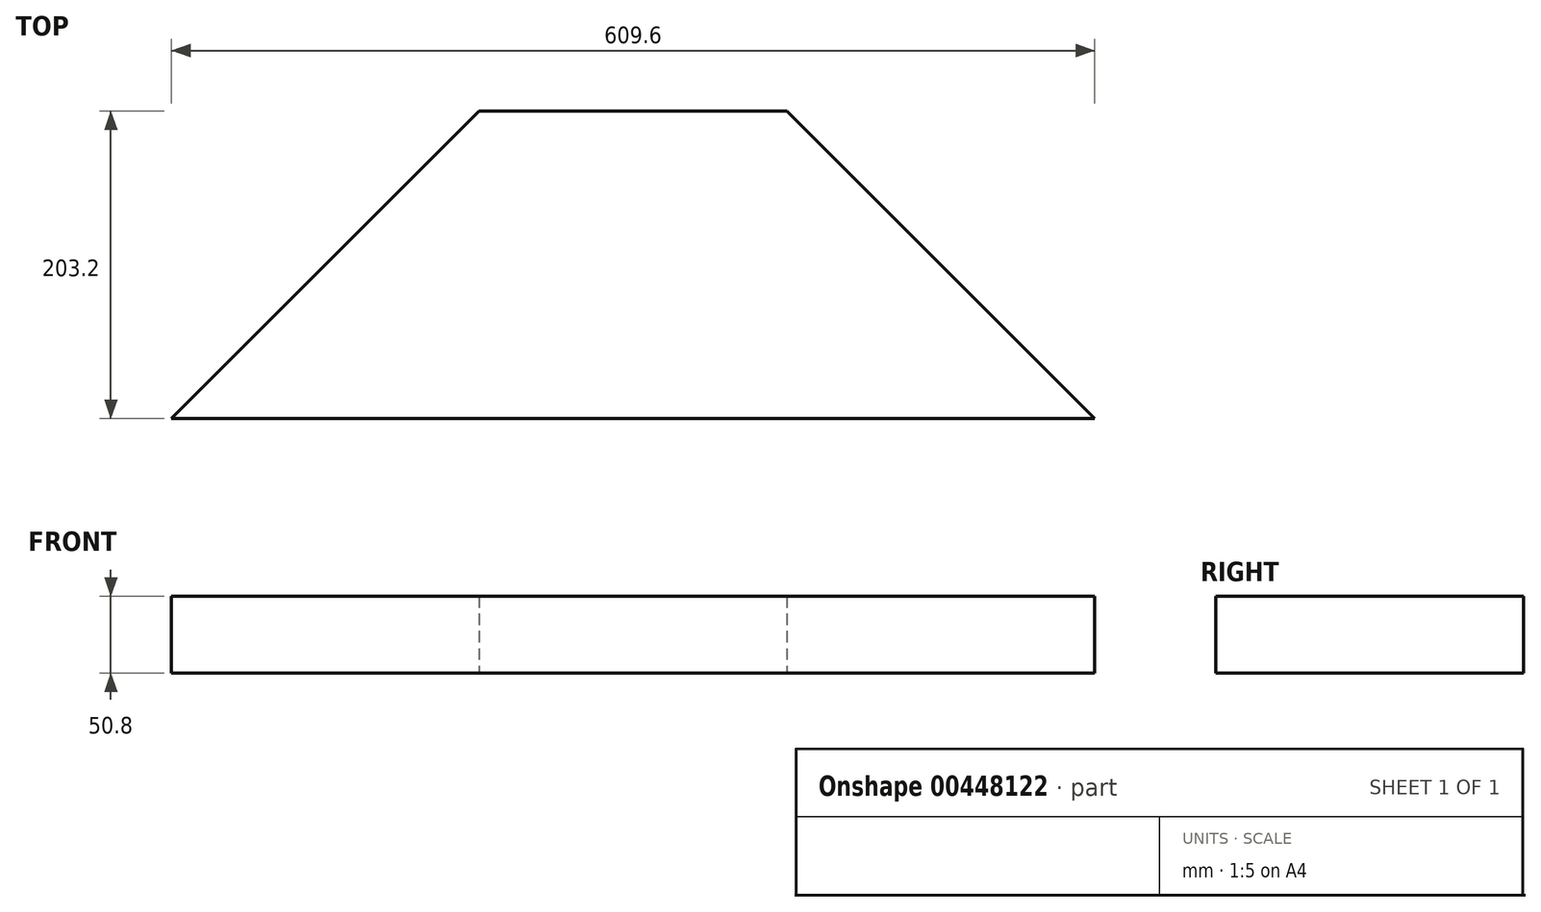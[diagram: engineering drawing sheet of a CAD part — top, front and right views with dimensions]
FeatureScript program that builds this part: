
annotation { "Feature Type Name" : "Feature", "Feature Type Description" : "" }
export const myFeature = defineFeature(function(context is Context, id is Id, definition is map)
    precondition{}
    {
        {
            var Q0;
            Q0=qCreatedBy(makeId("Top.planeOp"),FACE);
            var sketch = newSketch(context, id + "F0", { "sketchPlane" : qUnion([Q0])});
            skPoint(sketch, "E0", {"position": v(0, 203.2) * mm});
            skPoint(sketch, "E1", {"position": v(101.6, 203.2) * mm});
            skPoint(sketch, "E2", {"position": v(-101.6, 203.2) * mm});
            skPoint(sketch, "E3", {"position": v(304.8, 0) * mm});
            skPoint(sketch, "E4", {"position": v(-304.8, 0) * mm});
            skLineSegment(sketch, "E5", {"start": v(-101.6, 203.2) * mm, "end": v(101.6, 203.2) * mm});
            skLineSegment(sketch, "E6", {"start": v(304.8, 0) * mm, "end": v(-304.8, 0) * mm});
            skLineSegment(sketch, "E7", {"start": v(-304.8, 0) * mm, "end": v(-101.6, 203.2) * mm});
            skLineSegment(sketch, "E8", {"start": v(101.6, 203.2) * mm, "end": v(304.8, 0) * mm});
            skPoint(sketch, "E9", {"position": v(-203.2, 101.6) * mm});
            skPoint(sketch, "E10", {"position": v(203.2, 101.6) * mm});
            skSolve(sketch);
        }
        {
            var Q0;
            Q0=qCreatedBy(makeId("Right.planeOp"),FACE);
            var sketch = newSketch(context, id + "F1", { "sketchPlane" : qUnion([Q0])});
            skLineSegment(sketch, "E11", {"start": v(0, 0) * mm, "end": v(305.13, 152.96) * mm});
            skLineSegment(sketch, "E12", {"start": v(305.13, 152.96) * mm, "end": v(0, 152.96) * mm});
            skLineSegment(sketch, "E13", {"start": v(0, 152.96) * mm, "end": v(0, 0) * mm});
            skSolve(sketch);
        }
        {
            var Q0;
            {var subQ0=sQuery(id+"F1.wireOp",EDGE,"E11");Q0=makeQuery(id+"FYI99B2akjMyhfM_1.boolean.opBoolean","MERGE",FACE,{"derivedFrom":[makeQuery(id+"Fa1wFBmMVlfcbIP_1.boolean.opBoolean","COPY",FACE,{"derivedFrom":makeQuery(id+"Fa1wFBmMVlfcbIP_1.opExtrude","SWEPT_FACE",FACE,{"disambiguationData":[OSD([subQ0])]})}),makeQuery(id+"FYI99B2akjMyhfM_1.opExtrude","SWEPT_FACE",FACE,{"disambiguationData":[OSD([subQ0]),TDD([makeQuery(id+"F1.imprint","IMPRINT",EDGE,{"derivedFrom":subQ0})])]}),makeQuery(id+"FYI99B2akjMyhfM_1.opExtrude","SWEPT_FACE",FACE,{"disambiguationData":[OSD([subQ0]),TDD([makeQuery(id+"Fa1wFBmMVlfcbIP_1.boolean.opBoolean","COPY",EDGE,{"derivedFrom":makeQuery(id+"Fa1wFBmMVlfcbIP_1.opExtrude","CAP_EDGE",EDGE,{"disambiguationData":[OSD([subQ0])],"isStart":true})})])]})]});}
            var sketch = newSketch(context, id + "F2", { "sketchPlane" : qUnion([Q0])});
            skLineSegment(sketch, "E14", {"start": v(101.6, 227.3) * mm, "end": v(304.8, 0) * mm});
            skLineSegment(sketch, "E15", {"start": v(304.8, 0) * mm, "end": v(270.73, 0) * mm});
            skLineSegment(sketch, "E16", {"start": v(270.73, 0) * mm, "end": v(67.53, 227.3) * mm});
            skLineSegment(sketch, "E17", {"start": v(67.53, 227.3) * mm, "end": v(101.6, 227.3) * mm});
            skSolve(sketch);
        }
        {
            var Q0;
            {var subQ0=sQuery(id+"F1.wireOp",EDGE,"E11");Q0=makeQuery(id+"FYI99B2akjMyhfM_1.boolean.opBoolean","MERGE",FACE,{"derivedFrom":[makeQuery(id+"Fa1wFBmMVlfcbIP_1.boolean.opBoolean","COPY",FACE,{"derivedFrom":makeQuery(id+"Fa1wFBmMVlfcbIP_1.opExtrude","SWEPT_FACE",FACE,{"disambiguationData":[OSD([subQ0])]})}),makeQuery(id+"FYI99B2akjMyhfM_1.opExtrude","SWEPT_FACE",FACE,{"disambiguationData":[OSD([subQ0]),TDD([makeQuery(id+"F1.imprint","IMPRINT",EDGE,{"derivedFrom":subQ0})])]}),makeQuery(id+"FYI99B2akjMyhfM_1.opExtrude","SWEPT_FACE",FACE,{"disambiguationData":[OSD([subQ0]),TDD([makeQuery(id+"Fa1wFBmMVlfcbIP_1.boolean.opBoolean","COPY",EDGE,{"derivedFrom":makeQuery(id+"Fa1wFBmMVlfcbIP_1.opExtrude","CAP_EDGE",EDGE,{"disambiguationData":[OSD([subQ0])],"isStart":true})})])]})]});}
            var sketch = newSketch(context, id + "F3", { "sketchPlane" : qUnion([Q0])});
            skLineSegment(sketch, "E18", {"start": v(-101.6, 227.3) * mm, "end": v(-304.8, 0) * mm});
            skLineSegment(sketch, "E19", {"start": v(-304.8, 0) * mm, "end": v(-270.73, 0) * mm});
            skLineSegment(sketch, "E20", {"start": v(-270.73, 0) * mm, "end": v(-67.53, 227.3) * mm});
            skLineSegment(sketch, "E21", {"start": v(-67.53, 227.3) * mm, "end": v(-101.6, 227.3) * mm});
            skSolve(sketch);
        }
        {
            var Q0;
            Q0 = qSketchRegion(id + "F0", true);
            extrude(context, id + "F4", {"entities" : qUnion([Q0]), "depth" : 50.8 * mm});
        }
    });
